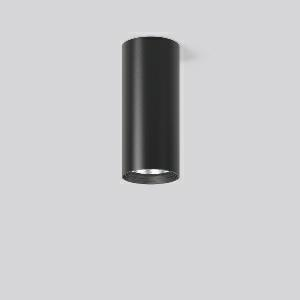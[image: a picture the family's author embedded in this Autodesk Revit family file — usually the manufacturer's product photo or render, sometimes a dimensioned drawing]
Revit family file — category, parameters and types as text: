
# Revit family: heledon_mini_a_931201_003_2_28c3
name_source: partatom
category: Lighting Fixtures
units: mm (PartAtom-declared; Revit-internal decimal feet)

## family parameters
Cut with Voids When Loaded = No
Host = Face
Light Source = No
Part Type = Normal
Room Calculation Point = No
Round Connector Dimension = Use Diameter
Shared = No

## types (1)
- HELEDON mini A (1 x LED Modul 927, 2300 lm, 2700)
    Apparent Load = 20 VA
    Approval mark = CE
    CIE Flux Codes = 99 100 100 100 100
    Color Rendering = 92
    Color Temperature = 2700
    Default Elevation = 1800 mm
    Description = Series: HELEDON mini
Cylindrical surface-mounted downlight. Housing: die-cast aluminium, powder-coated. Internal ceiling frame polycarbonate with bayonet mounting. Black plastic ring and recessed LED to prevent glare from the side. Optical assembly with reflector made of MIRO-Silver with 98% total light reflection for outstanding efficiency - can be changed without tools. Best colour rendering index Ra>90. Suitable for Ceiling mounting. Easy installation with a separate ceiling frame with bayonet mounting and plug connection. Driver integrated. Connected via plug-in connector. High quality converter without flickering and stroboscopic effect. The following accessories can be mounted without use of tools: interchangeable lenses, decorative glasses, honeycomb louvre, clear and frosted diffusers, white interchangeable plastic ring. 
Colour: deep black, matt (RAL 9005)
Diameter: 87 mm
Height: 197 mm
Lamp: LED
Socket: without socket
Colour temperature: 2700K
Colour rendering index (CRI): 92
System power: 20 W
Rated luminous flux: 2300 lm
Luminous efficiency: 115 lm/W
Control gear: Regulated power supply
Protection class: I
Type of protection: IP 20
    Height = 197 mm
    Lamp = 1 x LED Modul 927
    Lamp Light Flux = 2300 lm
    Lamp count = 1
    Length = 87 mm
    Lifetime = 50000 h
    Luminous efficacy = 115 lm/W
    Manufacturer = RZB
    ModVariant = No
    Model = 931201.003.2
    Mounting Place = Ceiling
    Mounting Type = Surface mounted
    Number of Poles = 1
    OnlyDefault = Yes
    Power Factor = 1
    Product Name = HELEDON mini A
    Product group = Surface mounted downlights
    ProductGroupID = 302
    Protection Class = Protection class I
    Protection Degree = IP 20
    RLX_Detail_Level = 1
    RLX_Emergency_Light_Flux = 0 lm
    RLX_Emergency_Type = 0
    RLX_Emergency_Type_DB = No
    RlxData = <blob elided: 106417 chars, md5=0715449e>
    Socket = socket
    Standby Power = 0 W
    System Light Flux = 2300 lm
    System Power = 20 W
    Type Comments = Product without accessories
    Type Image = 931188.003.jpg
    URL = http://relux.com
    VarID = ---
    Voltage = 230 V
    Voltage Range = 220-240 V
    Weight = 0.00 kg
    Width = 0 mm  [stored 0 ft]

note: [stored X ft] marks values corroborated as IEEE doubles in the binary element streams (Revit-internal decimal feet)

## geometry (parser evidence)
native form markers: Blend x4, Sweep x9
no freeform markers — native parametric forms only
